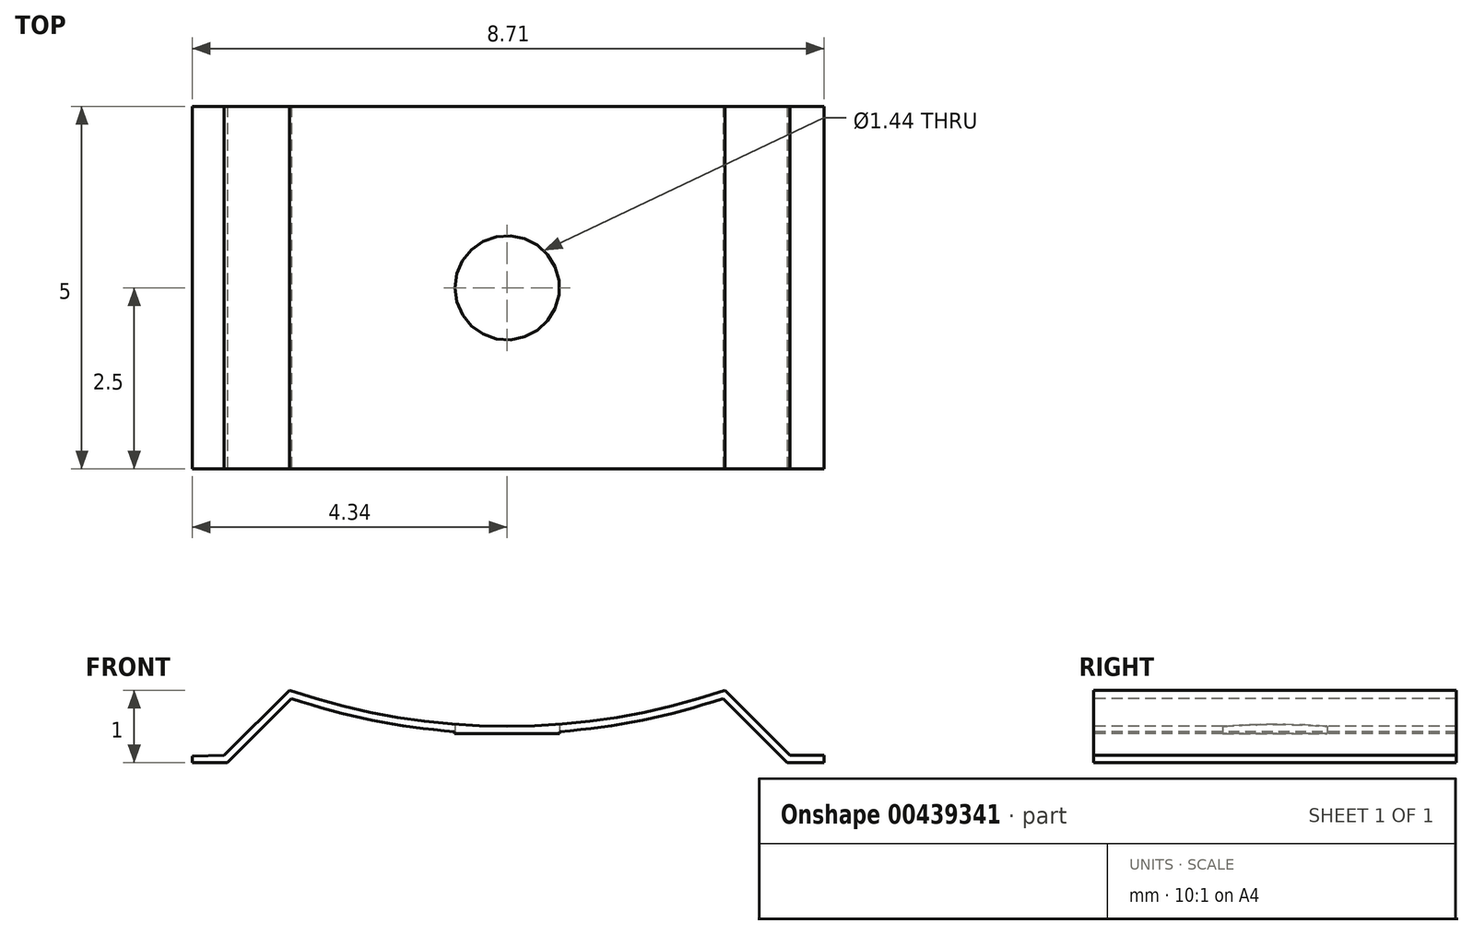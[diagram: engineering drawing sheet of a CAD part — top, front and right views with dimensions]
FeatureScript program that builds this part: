
annotation { "Feature Type Name" : "Feature", "Feature Type Description" : "" }
export const myFeature = defineFeature(function(context is Context, id is Id, definition is map)
    precondition{}
    {
        {
            var Q0;
            Q0=qCreatedBy(makeId("Top.planeOp"),FACE);
            var sketch = newSketch(context, id + "F0", { "sketchPlane" : qUnion([Q0])});
            skLineSegment(sketch, "E0.bottom", {"start": v(0, 5) * mm, "end": v(10, 5) * mm});
            skLineSegment(sketch, "E0.top", {"start": v(0, 0) * mm, "end": v(10, 0) * mm});
            skLineSegment(sketch, "E0.left", {"start": v(0, 5) * mm, "end": v(0, 0) * mm});
            skLineSegment(sketch, "E0.right", {"start": v(10, 5) * mm, "end": v(10, 0) * mm});
            skPoint(sketch, "E1.centerSnap0", {"position": v(0, 2.5) * mm});
            skPoint(sketch, "E1.centerSnap1", {"position": v(5, 0) * mm});
            skSolve(sketch);
        }
        {
            var Q0;
            Q0=makeQuery(id+"F0.imprint","IMPRINT",FACE,{"disambiguationData":[TD([[makeQuery(id+"F0.imprint","IMPRINT",EDGE,{"derivedFrom":sQuery(id+"F0.wireOp",EDGE,"E0.bottom")}),-1.0]])]});
            extrude(context, id + "F1", {"entities" : qUnion([Q0]), "depth" : 1 * mm});
        }
        {
            var Q0;
            Q0=makeQuery(id+"F1.opExtrude","CAP_EDGE",EDGE,{"disambiguationData":[OSD([sQuery(id+"F0.wireOp",EDGE,"E0.left")])],"isStart":false});
            var Q1;
            Q1=makeQuery(id+"F1.opExtrude","CAP_EDGE",EDGE,{"disambiguationData":[OSD([sQuery(id+"F0.wireOp",EDGE,"E0.right")])],"isStart":false});
            chamfer(context, id + "F2", {"entities" : qUnion([Q0, Q1]), "width" : 2 * mm, "tangentPropagation" : true});
        }
        {
            var Q0;
            Q0=makeQuery(id+"F1.opExtrude","SWEPT_FACE",FACE,{"disambiguationData":[OSD([sQuery(id+"F0.wireOp",EDGE,"E0.top")])]});
            var sketch = newSketch(context, id + "F3", { "sketchPlane" : qUnion([Q0])});
            skPoint(sketch, "E2.startSnap0", {"position": v(5, 1) * mm});
            skLineSegment(sketch, "E3", {"start": v(5, 1) * mm, "end": v(5, 0.5) * mm});
            skArc(sketch, "E4", {"start": v(2, 1) * mm, "mid": v(5, 0.5) * mm, "end": v(8, 1) * mm});
            skLineSegment(sketch, "E5.0", {"start": v(2.03, 0.89) * mm, "end": v(1.07, -0.07) * mm});
            skArc(sketch, "E5.1", {"start": v(2.03, 0.89) * mm, "mid": v(5, 0.4) * mm, "end": v(7.97, 0.89) * mm});
            skLineSegment(sketch, "E5.2", {"start": v(8.93, -0.07) * mm, "end": v(7.97, 0.89) * mm});
            skSolve(sketch);
        }
        {
            var Q0;
            {var subQ0=sQuery(id+"F3.wireOp",EDGE,"E3");Q0=makeQuery(id+"F3.imprint","IMPRINT",FACE,{"disambiguationData":[TD([[makeQuery(id+"F3.imprint","IMPRINT",EDGE,{"derivedFrom":subQ0}),-1.0]])]});}
            var Q1;
            {var subQ0=sQuery(id+"F3.wireOp",EDGE,"E3");Q1=makeQuery(id+"F3.imprint","IMPRINT",FACE,{"disambiguationData":[TD([[makeQuery(id+"F3.imprint","IMPRINT",EDGE,{"derivedFrom":subQ0}),1.0]])]});}
            var Q2;
            {var subQ0=sQuery(id+"F3.wireOp",EDGE,"E5.1");Q2=makeQuery(id+"F3.imprint","IMPRINT",FACE,{"disambiguationData":[TD([[makeQuery(id+"F3.imprint","IMPRINT",EDGE,{"derivedFrom":subQ0}),-1.0]])]});}
            extrude(context, id + "F4", {"entities" : qUnion([Q0, Q1, Q2]), "operationType" : NewBodyOperationType.REMOVE, "oppositeDirection" : true, "depth" : 25 * mm});
        }
        {
            var Q0;
            Q0=makeQuery(id+"F1.opExtrude","SWEPT_FACE",FACE,{"disambiguationData":[OSD([sQuery(id+"F0.wireOp",EDGE,"E0.top")])]});
            var sketch = newSketch(context, id + "F5", { "sketchPlane" : qUnion([Q0])});
            skLineSegment(sketch, "E6", {"start": v(1.14, 0) * mm, "end": v(1.14, 0.1) * mm});
            skLineSegment(sketch, "E7", {"start": v(1.14, 0.1) * mm, "end": v(0.66, 0.1) * mm});
            skLineSegment(sketch, "E8", {"start": v(0.66, 0.1) * mm, "end": v(0.66, 0) * mm});
            skLineSegment(sketch, "E9", {"start": v(0.66, 0) * mm, "end": v(1.14, 0) * mm});
            skLineSegment(sketch, "E10", {"start": v(8.86, 0) * mm, "end": v(8.86, 0.1) * mm});
            skLineSegment(sketch, "E11", {"start": v(8.86, 0.1) * mm, "end": v(9.37, 0.1) * mm});
            skLineSegment(sketch, "E12", {"start": v(9.37, 0.1) * mm, "end": v(9.37, 0) * mm});
            skLineSegment(sketch, "E13", {"start": v(9.37, 0) * mm, "end": v(8.86, 0) * mm});
            skSolve(sketch);
        }
        {
            var Q0;
            {var subQ0=sQuery(id+"F5.wireOp",EDGE,"E12");Q0=makeQuery(id+"F5.imprint","IMPRINT",FACE,{"disambiguationData":[TD([[makeQuery(id+"F5.imprint","IMPRINT",EDGE,{"derivedFrom":subQ0}),-1.0]])]});}
            var Q1;
            {var subQ0=sQuery(id+"F5.wireOp",EDGE,"E8");Q1=makeQuery(id+"F5.imprint","IMPRINT",FACE,{"disambiguationData":[TD([[makeQuery(id+"F5.imprint","IMPRINT",EDGE,{"derivedFrom":subQ0}),1.0]])]});}
            extrude(context, id + "F6", {"entities" : qUnion([Q0, Q1]), "operationType" : NewBodyOperationType.ADD, "oppositeDirection" : true, "depth" : 5 * mm});
        }
        {
            var Q0;
            {var subQ0=sQuery(id+"F0.wireOp",EDGE,"E0.top");Q0=makeQuery(id+"F6.boolean.opBoolean","MERGE",FACE,{"derivedFrom":[makeQuery(id+"F1.opExtrude","SWEPT_FACE",FACE,{"disambiguationData":[OSD([subQ0])]}),makeQuery(id+"F6.opExtrude","CAP_FACE",FACE,{"disambiguationData":[OSD([subQ0,sQuery(id+"F0.wireOp",EDGE,"E0.left"),sQuery(id+"F5.wireOp",EDGE,"E7"),sQuery(id+"F5.wireOp",EDGE,"E8"),sQuery(id+"F5.wireOp",EDGE,"E9")])],"isStart":true}),makeQuery(id+"F6.opExtrude","CAP_FACE",FACE,{"disambiguationData":[OSD([subQ0,sQuery(id+"F0.wireOp",EDGE,"E0.right"),sQuery(id+"F5.wireOp",EDGE,"E11"),sQuery(id+"F5.wireOp",EDGE,"E12"),sQuery(id+"F5.wireOp",EDGE,"E13")])],"isStart":true})]});}
            var sketch = newSketch(context, id + "F7", { "sketchPlane" : qUnion([Q0])});
            skLineSegment(sketch, "E14", {"start": v(5, 0.4) * mm, "end": v(5.73, 0.4) * mm});
            skLineSegment(sketch, "E15", {"start": v(5, 0.4) * mm, "end": v(4.28, 0.4) * mm});
            skLineSegment(sketch, "E16", {"start": v(4.28, 0.4) * mm, "end": v(4.28, 0.43) * mm});
            skLineSegment(sketch, "E17", {"start": v(4.28, 0.43) * mm, "end": v(5.73, 0.43) * mm});
            skLineSegment(sketch, "E18", {"start": v(5.73, 0.43) * mm, "end": v(5.73, 0.4) * mm});
            skSolve(sketch);
        }
        {
            var Q0;
            {var subQ0=sQuery(id+"F7.wireOp",EDGE,"E15");Q0=makeQuery(id+"F7.imprint","IMPRINT",FACE,{"disambiguationData":[TD([[makeQuery(id+"F7.imprint","IMPRINT",EDGE,{"derivedFrom":subQ0}),-1.0]])]});}
            var Q1;
            {var subQ0=sQuery(id+"F7.wireOp",EDGE,"E14");Q1=makeQuery(id+"F7.imprint","IMPRINT",FACE,{"disambiguationData":[TD([[makeQuery(id+"F7.imprint","IMPRINT",EDGE,{"derivedFrom":subQ0}),1.0]])]});}
            extrude(context, id + "F8", {"entities" : qUnion([Q0, Q1]), "operationType" : NewBodyOperationType.ADD, "oppositeDirection" : true, "depth" : 5 * mm});
        }
        {
            var Q0;
            Q0=makeQuery(id+"F8.boolean.opBoolean","MERGE",FACE,{"derivedFrom":[makeQuery(id+"F8.opExtrude","SWEPT_FACE",FACE,{"disambiguationData":[OSD([sQuery(id+"F7.wireOp",EDGE,"E14")])]}),makeQuery(id+"F8.opExtrude","SWEPT_FACE",FACE,{"disambiguationData":[OSD([sQuery(id+"F7.wireOp",EDGE,"E15")])]})]});
            var sketch = newSketch(context, id + "F9", { "sketchPlane" : qUnion([Q0])});
            skCircle(sketch, "E19", {"center": v(5, -2.5) * mm, "radius": 0.72 * mm});
            skPoint(sketch, "E19.centerSnap0", {"position": v(4.28, -2.5) * mm});
            skPoint(sketch, "E19.centerSnap1", {"position": v(5, 0) * mm});
            skSolve(sketch);
        }
        {
            var Q0;
            Q0 = qSketchRegion(id + "F9", true);
            extrude(context, id + "F10", {"entities" : qUnion([Q0]), "operationType" : NewBodyOperationType.REMOVE, "oppositeDirection" : true, "depth" : 1 * mm});
        }
    });
